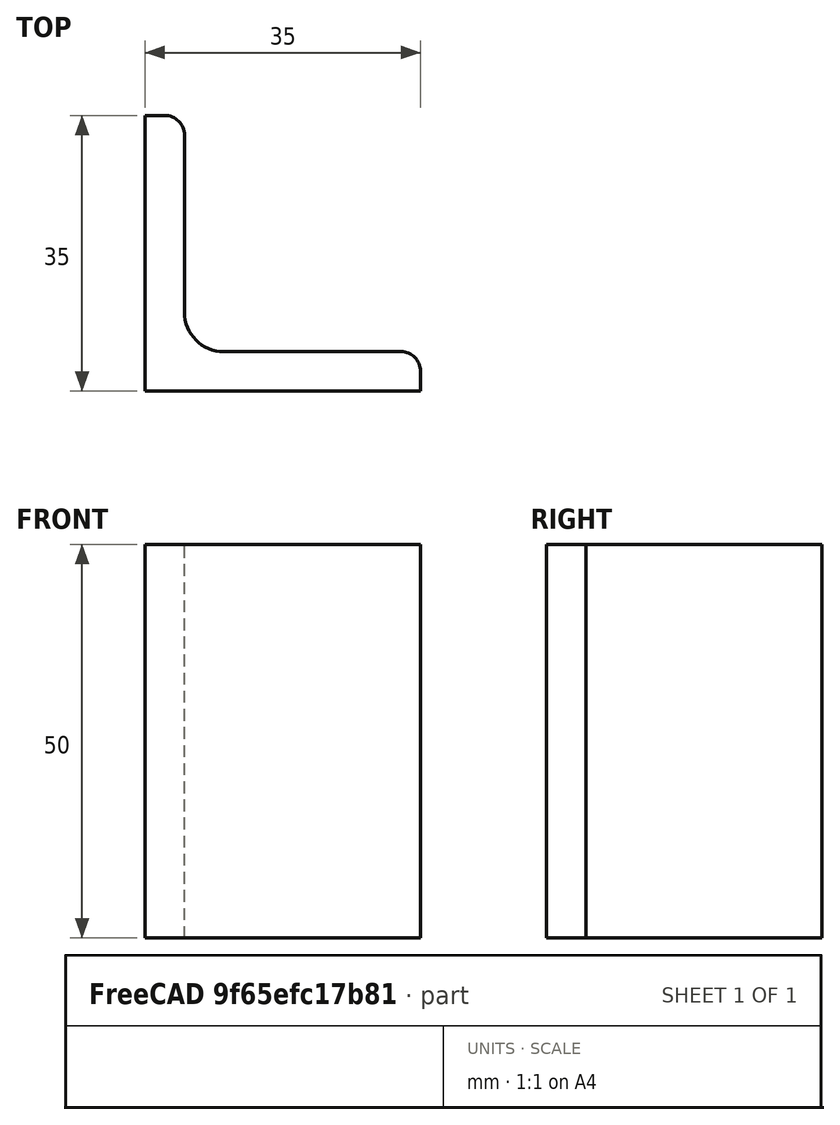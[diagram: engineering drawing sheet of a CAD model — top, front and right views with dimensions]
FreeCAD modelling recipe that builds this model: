
FCSTD DOCUMENT  (FreeCAD 0.15R4671 (Git))
Label: Angle Bar L35x35x5 EN10056 S235JR
License: All rights reserved
LicenseURL: http://en.wikipedia.org/wiki/All_rights_reserved
objects: Sketcher::SketchObject×1, Part::Extrusion×1
note: 2 computed .brp shape members not serialized (recipe doc carries the construction recipe); baked Part::Feature solids carry a one-line shape summary decoded from their .brp

FEATURE [Sketcher::SketchObject] Sketch
  sketch-geometry (9):
    g0: LineSegment StartX=0 StartY=0 StartZ=0 EndX=35 EndY=0 EndZ=0
    g1: LineSegment StartX=35 StartY=0 StartZ=0 EndX=35 EndY=2.5 EndZ=0
    g2: LineSegment StartX=32.5 StartY=5 StartZ=0 EndX=10 EndY=5 EndZ=0
    g3: LineSegment StartX=0 StartY=0 StartZ=0 EndX=0 EndY=35 EndZ=0
    g4: LineSegment StartX=0 StartY=35 StartZ=0 EndX=2.5 EndY=35 EndZ=0
    g5: LineSegment StartX=5 StartY=32.5 StartZ=0 EndX=5 EndY=10 EndZ=0
    g6: ArcOfCircle CenterX=10 CenterY=10 CenterZ=0 NormalX=0 NormalY=0 NormalZ=1 Radius=5 StartAngle=3.14159 EndAngle=4.71239
    g7: ArcOfCircle CenterX=2.5 CenterY=32.5 CenterZ=0 NormalX=0 NormalY=0 NormalZ=1 Radius=2.5 StartAngle=0 EndAngle=1.5708
    g8: ArcOfCircle CenterX=32.5 CenterY=2.5 CenterZ=0 NormalX=0 NormalY=0 NormalZ=1 Radius=2.5 StartAngle=0 EndAngle=1.5708
  constraints (23):
    c: Coincident(g0,g-1)
    c: Horizontal(g0)
    c: Coincident(g1,g0)
    c: Vertical(g1)
    c: Horizontal(g2)
    c: Coincident(g3,g-1)
    c: Vertical(g3)
    c: Coincident(g4,g3)
    c: Horizontal(g4)
    c: Vertical(g5)
    c: Tangent(g5,g6) = -1.5708
    c: Tangent(g2,g6) = 1.5708
    c: Tangent(g4,g7) = 1.5708
    c: Tangent(g5,g7) = 1.5708
    c: Tangent(g2,g8) = -1.5708
    c: Tangent(g1,g8) = -1.5708
    c: DistanceX(g0) = 35
    c: DistanceY(g3) = 35
    c: DistanceY(g0,g2) = 5
    c: DistanceX(g3,g5) = 5
    c: Radius(g6) = 5
    c: Radius(g8) = 2.5
    c: Radius(g7) = 2.5
FEATURE [Part::Extrusion] Extrude  label="Angle Bar L35x35x5 EN10056 S235JR"
  Base = -> Sketch
  Dir = (0,0,50)
  Solid = true
